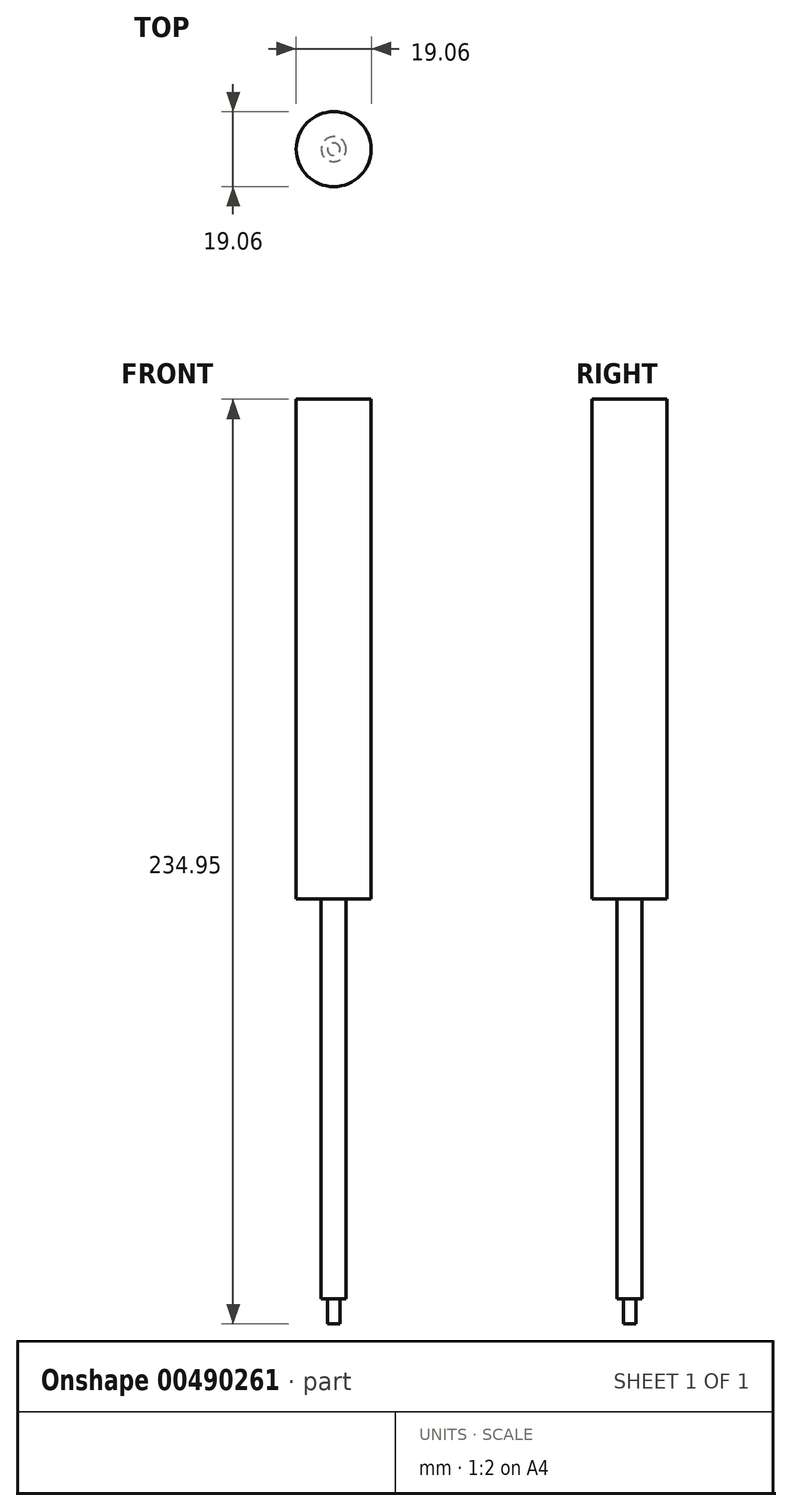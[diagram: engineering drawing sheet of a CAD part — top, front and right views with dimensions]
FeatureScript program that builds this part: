
annotation { "Feature Type Name" : "Feature", "Feature Type Description" : "" }
export const myFeature = defineFeature(function(context is Context, id is Id, definition is map)
    precondition{}
    {
        {
            var Q0;
            Q0=qCreatedBy(makeId("Top.planeOp"),FACE);
            var sketch = newSketch(context, id + "F0", { "sketchPlane" : qUnion([Q0])});
            skCircle(sketch, "E0", {"center": v(0, 0) * mm, "radius": 9.53 * mm});
            skCircle(sketch, "E1", {"center": v(0, 0) * mm, "radius": 3.18 * mm});
            skSolve(sketch);
        }
        {
            var Q0;
            Q0=makeQuery(id+"F0.imprint","IMPRINT",FACE,{"disambiguationData":[TD([[makeQuery(id+"F0.imprint","IMPRINT",EDGE,{"derivedFrom":sQuery(id+"F0.wireOp",EDGE,"E0")}),1.0]])]});
            var Q1;
            Q1=makeQuery(id+"F0.imprint","IMPRINT",FACE,{"disambiguationData":[TD([[makeQuery(id+"F0.imprint","IMPRINT",EDGE,{"derivedFrom":sQuery(id+"F0.wireOp",EDGE,"E1")}),1.0]])]});
            extrude(context, id + "F1", {"entities" : qUnion([Q0, Q1]), "depth" : 127 * mm});
        }
        {
            var Q0;
            Q0=makeQuery(id+"F0.imprint","IMPRINT",FACE,{"disambiguationData":[TD([[makeQuery(id+"F0.imprint","IMPRINT",EDGE,{"derivedFrom":sQuery(id+"F0.wireOp",EDGE,"E1")}),1.0]])]});
            extrude(context, id + "F2", {"entities" : qUnion([Q0]), "operationType" : NewBodyOperationType.ADD, "oppositeDirection" : true, "depth" : 101.6 * mm});
        }
        {
            var Q0;
            Q0=makeQuery(id+"F2.opExtrude","CAP_FACE",FACE,{"disambiguationData":[OSD([sQuery(id+"F0.wireOp",EDGE,"E1")])],"isStart":false});
            var sketch = newSketch(context, id + "F3", { "sketchPlane" : qUnion([Q0])});
            skCircle(sketch, "E2", {"center": v(0, 0) * mm, "radius": 1.59 * mm});
            skSolve(sketch);
        }
        {
            var Q0;
            Q0=makeQuery(id+"F3.imprint","IMPRINT",FACE,{"disambiguationData":[TD([[makeQuery(id+"F3.imprint","IMPRINT",EDGE,{"derivedFrom":sQuery(id+"F3.wireOp",EDGE,"E2")}),1.0]])]});
            extrude(context, id + "F4", {"entities" : qUnion([Q0]), "operationType" : NewBodyOperationType.ADD, "depth" : 6.35 * mm});
        }
    });
